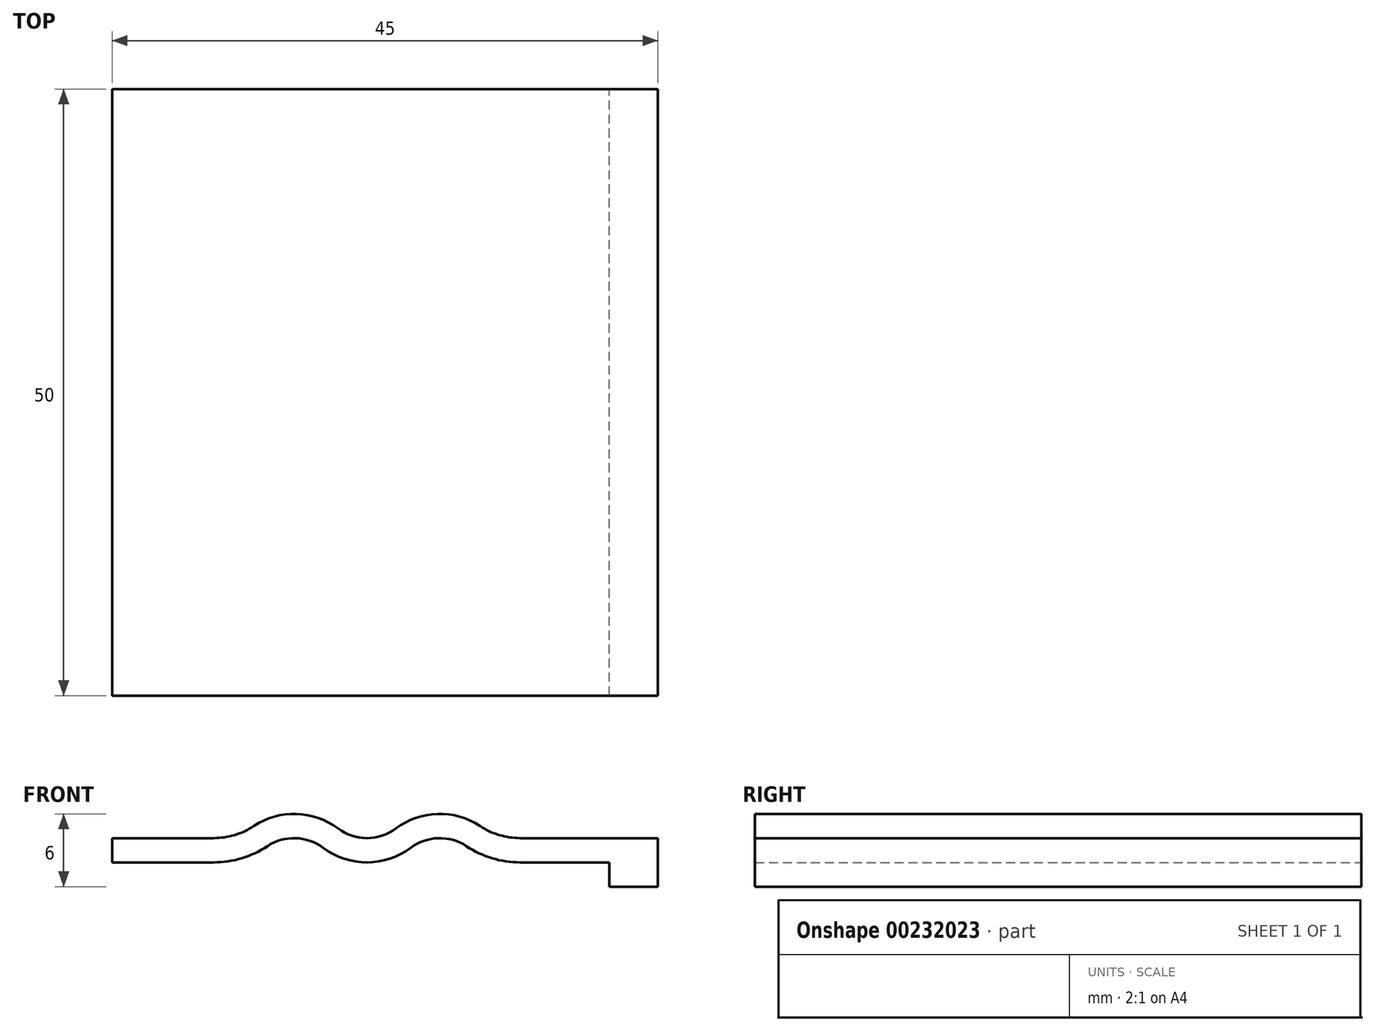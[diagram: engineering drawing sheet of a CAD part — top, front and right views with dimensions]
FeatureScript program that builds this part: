
annotation { "Feature Type Name" : "Feature", "Feature Type Description" : "" }
export const myFeature = defineFeature(function(context is Context, id is Id, definition is map)
    precondition{}
    {
        {
            var Q0;
            Q0=qCreatedBy(makeId("Front.planeOp"),FACE);
            var sketch = newSketch(context, id + "F0", { "sketchPlane" : qUnion([Q0])});
            skLineSegment(sketch, "E0", {"start": v(0, 0) * mm, "end": v(-11.37, 0) * mm});
            skLineSegment(sketch, "E1", {"start": v(-18, -28.52) * mm, "end": v(-18, 33.13) * mm, "construction": true});
            skLineSegment(sketch, "E2", {"start": v(-30, 34.87) * mm, "end": v(-30, -30.26) * mm, "construction": true});
            skArc(sketch, "E3", {"start": v(-14.68, 1) * mm, "mid": v(-18.17, 2) * mm, "end": v(-21.6, 0.8) * mm});
            skArc(sketch, "E4", {"start": v(-26.4, 0.8) * mm, "mid": v(-29.83, 2) * mm, "end": v(-33.32, 1) * mm});
            skArc(sketch, "E5", {"start": v(-26.4, 0.8) * mm, "mid": v(-24, 0) * mm, "end": v(-21.6, 0.8) * mm});
            skPoint(sketch, "E5.first.point", {"position": v(-26.4, 0.8) * mm});
            skPoint(sketch, "E5.second.point", {"position": v(-21.6, 0.8) * mm});
            skPoint(sketch, "E5.third.point", {"position": v(-23.13, 7.9) * mm});
            skLineSegment(sketch, "E6", {"start": v(-36.63, 0) * mm, "end": v(-45, 0) * mm});
            skPoint(sketch, "E7.visualSharp", {"position": v(-13.53, 0) * mm});
            skArc(sketch, "E7.filletArc", {"start": v(-14.68, 1) * mm, "mid": v(-13.1, 0.26) * mm, "end": v(-11.37, 0) * mm});
            skPoint(sketch, "E8.visualSharp", {"position": v(-34.47, 0) * mm});
            skArc(sketch, "E8.filletArc", {"start": v(-36.63, 0) * mm, "mid": v(-34.9, 0.26) * mm, "end": v(-33.32, 1) * mm});
            skLineSegment(sketch, "E9.0", {"start": v(-36.63, -2) * mm, "end": v(-45, -2) * mm});
            skArc(sketch, "E9.1", {"start": v(-36.63, -2) * mm, "mid": v(-34.32, -1.66) * mm, "end": v(-32.21, -0.67) * mm});
            skArc(sketch, "E9.2", {"start": v(-27.6, -0.8) * mm, "mid": v(-29.88, 0) * mm, "end": v(-32.21, -0.67) * mm});
            skLineSegment(sketch, "E9.3", {"start": v(-4, -2) * mm, "end": v(-11.37, -2) * mm});
            skArc(sketch, "E9.4", {"start": v(-15.79, -0.67) * mm, "mid": v(-13.68, -1.66) * mm, "end": v(-11.37, -2) * mm});
            skArc(sketch, "E9.5", {"start": v(-15.79, -0.67) * mm, "mid": v(-18.12, 0) * mm, "end": v(-20.4, -0.8) * mm});
            skArc(sketch, "E9.6", {"start": v(-27.6, -0.8) * mm, "mid": v(-24, -2) * mm, "end": v(-20.4, -0.8) * mm});
            skLineSegment(sketch, "E10", {"start": v(-45, 0) * mm, "end": v(-45, -2) * mm});
            skLineSegment(sketch, "E11.0", {"start": v(0, -4) * mm, "end": v(-4, -4) * mm});
            skLineSegment(sketch, "E12", {"start": v(0, 0) * mm, "end": v(0, -4) * mm});
            skLineSegment(sketch, "E13.0", {"start": v(-4, -2) * mm, "end": v(-4, -4) * mm});
            skSolve(sketch);
        }
        {
            var Q0;
            Q0=makeQuery(id+"F0.imprint","IMPRINT",FACE,{"disambiguationData":[TD([[makeQuery(id+"F0.imprint","IMPRINT",EDGE,{"derivedFrom":sQuery(id+"F0.wireOp",EDGE,"E0")}),1.0]])]});
            extrude(context, id + "F1", {"entities" : qUnion([Q0]), "depth" : 50 * mm});
        }
    });
